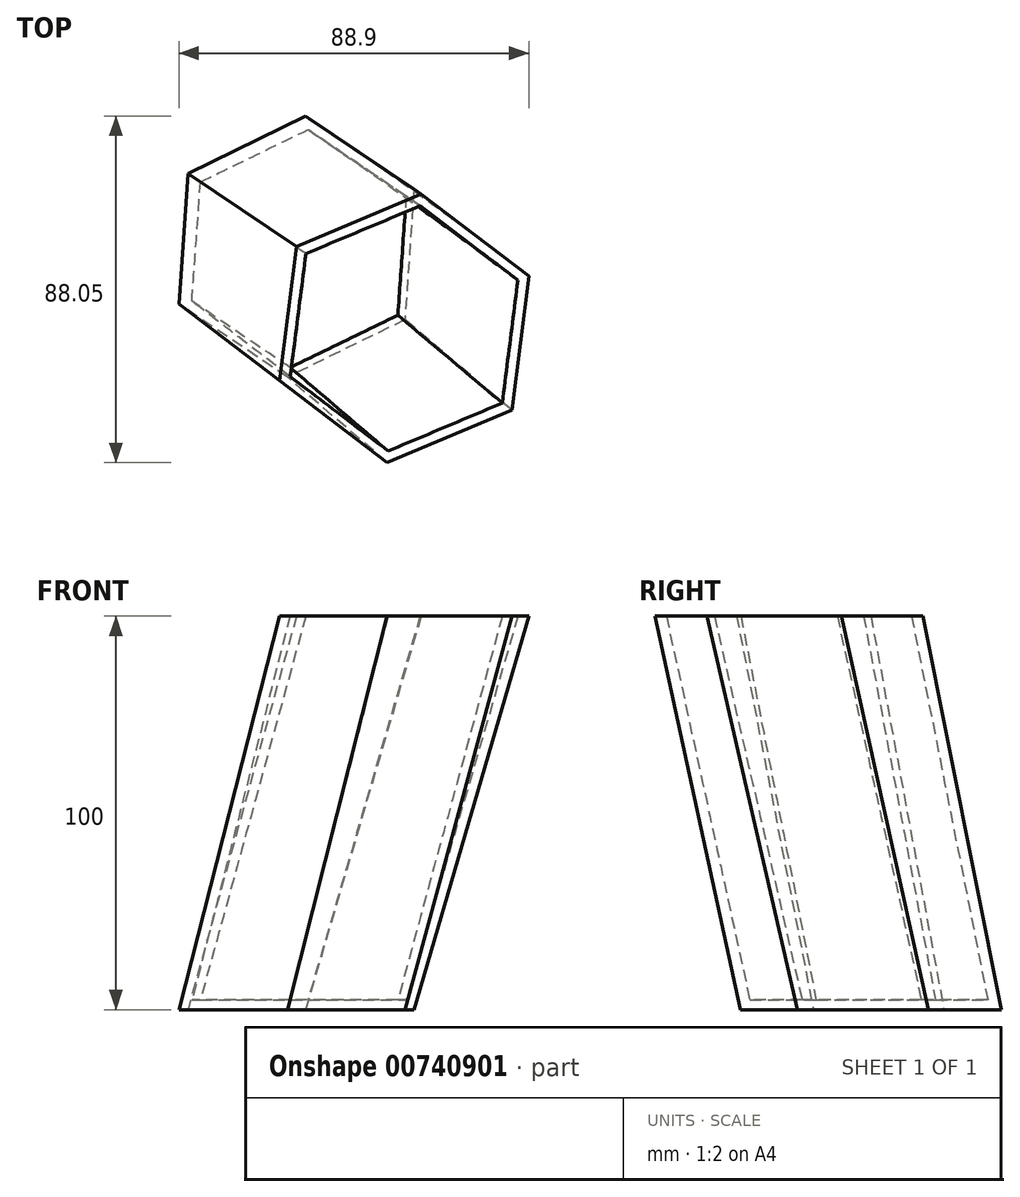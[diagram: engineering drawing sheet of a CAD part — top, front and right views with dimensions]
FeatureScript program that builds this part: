
annotation { "Feature Type Name" : "Feature", "Feature Type Description" : "" }
export const myFeature = defineFeature(function(context is Context, id is Id, definition is map)
    precondition{}
    {
        {
            var Q0;
            Q0=qCreatedBy(makeId("Top.planeOp"),FACE);
            cPlane(context, id + "F0", {"entities" : qUnion([Q0]), "cplaneType" : CPlaneType.OFFSET, "offset" : 100 * mm, "width" : 150 * mm, "height" : 150 * mm});
        }
        {
            var Q0;
            Q0=qCreatedBy(makeId("Top.planeOp"),FACE);
            var sketch = newSketch(context, id + "F1", { "sketchPlane" : qUnion([Q0])});
            skCircle(sketch, "E0.cCircle", {"center": v(0, 0) * mm, "radius": 33.25 * mm, "construction": true});
            skLineSegment(sketch, "E0.0", {"start": v(-29.87, -14.59) * mm, "end": v(-27.57, 18.58) * mm});
            skLineSegment(sketch, "E0.1", {"start": v(-27.57, 18.58) * mm, "end": v(2.3, 33.17) * mm});
            skLineSegment(sketch, "E0.2", {"start": v(2.3, 33.17) * mm, "end": v(29.87, 14.59) * mm});
            skLineSegment(sketch, "E0.3", {"start": v(29.87, 14.59) * mm, "end": v(27.57, -18.58) * mm});
            skLineSegment(sketch, "E0.4", {"start": v(27.57, -18.58) * mm, "end": v(-2.3, -33.17) * mm});
            skLineSegment(sketch, "E0.5", {"start": v(-2.3, -33.17) * mm, "end": v(-29.87, -14.59) * mm});
            skSolve(sketch);
        }
        {
            var Q0;
            Q0=qCreatedBy(id+"F0.planeOp",FACE);
            var sketch = newSketch(context, id + "F2", { "sketchPlane" : qUnion([Q0])});
            skCircle(sketch, "E1.cCircle", {"center": v(27.35, -20.8) * mm, "radius": 34.36 * mm, "construction": true});
            skLineSegment(sketch, "E1.0", {"start": v(0, 0) * mm, "end": v(31.68, 13.3) * mm});
            skLineSegment(sketch, "E1.1", {"start": v(31.68, 13.3) * mm, "end": v(59.03, -7.5) * mm});
            skLineSegment(sketch, "E1.2", {"start": v(59.03, -7.5) * mm, "end": v(54.7, -41.59) * mm});
            skLineSegment(sketch, "E1.3", {"start": v(54.7, -41.59) * mm, "end": v(23.02, -54.88) * mm});
            skLineSegment(sketch, "E1.4", {"start": v(23.02, -54.88) * mm, "end": v(-4.33, -34.08) * mm});
            skLineSegment(sketch, "E1.5", {"start": v(-4.33, -34.08) * mm, "end": v(0, 0) * mm});
            skSolve(sketch);
        }
        {
            var Q0;
            Q0=makeQuery(id+"F2.imprint","IMPRINT",FACE,{"disambiguationData":[TD([[makeQuery(id+"F2.imprint","IMPRINT",EDGE,{"derivedFrom":sQuery(id+"F2.wireOp",EDGE,"E1.0")}),-1.0]])]});
            var Q1;
            Q1 = qSketchRegion(id + "F1", true);
            loft(context, id + "F3", {"sheetProfilesArray" : [{ "sheetProfileEntities" : qUnion([Q0]) }, { "sheetProfileEntities" : qUnion([Q1]) }]});
        }
        {
            var Q0;
            Q0=makeQuery(id+"F3.opLoft","CAP_FACE",FACE,{"disambiguationData":[OSD([makeQuery(id+"F2.imprint","IMPRINT",FACE,{"disambiguationData":[TD([[makeQuery(id+"F2.imprint","IMPRINT",EDGE,{"derivedFrom":sQuery(id+"F2.wireOp",EDGE,"E1.0")}),-1.0]])]})])],"isStart":true});
            shell(context, id + "F4", {"entities" : qUnion([Q0]), "thickness" : 2.5 * mm});
        }
    });
